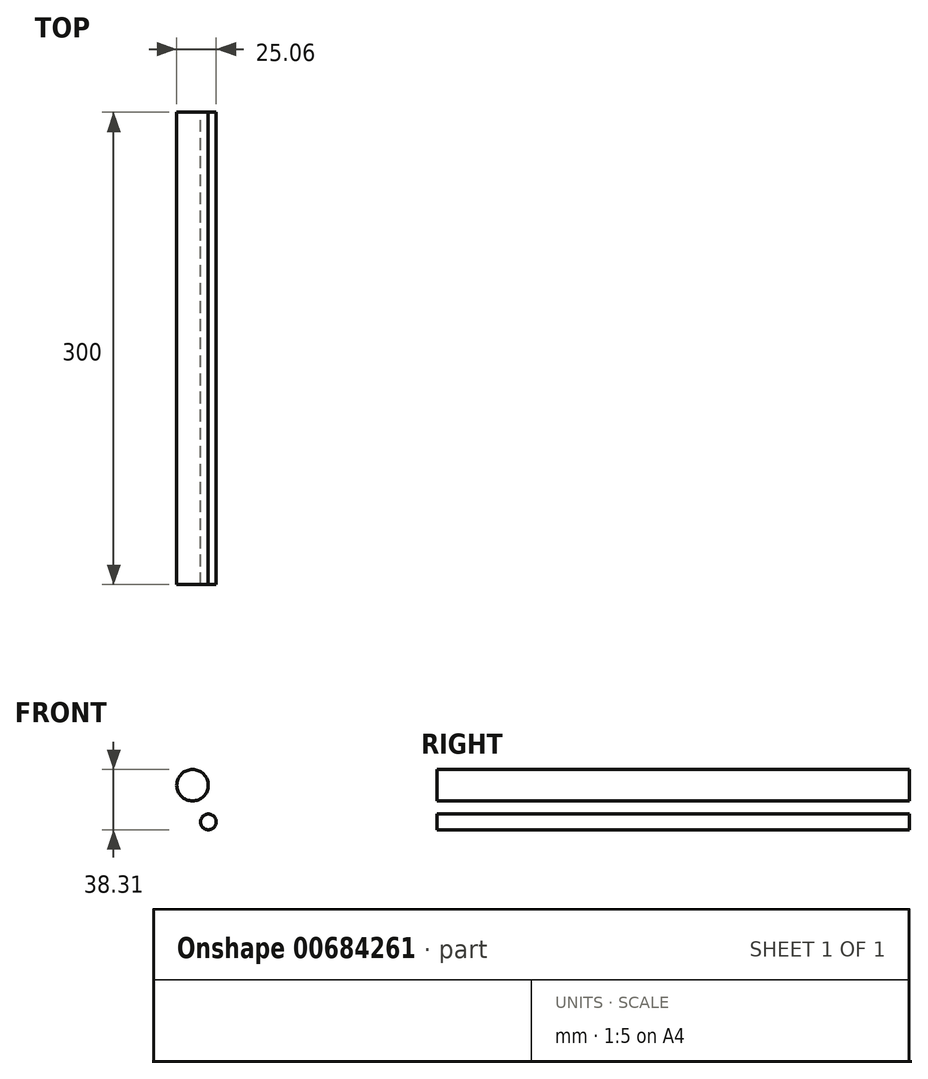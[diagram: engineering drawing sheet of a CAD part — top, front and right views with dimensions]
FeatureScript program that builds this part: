
annotation { "Feature Type Name" : "Feature", "Feature Type Description" : "" }
export const myFeature = defineFeature(function(context is Context, id is Id, definition is map)
    precondition{}
    {
        {
            var Q0;
            Q0=qCreatedBy(makeId("Front.planeOp"),FACE);
            var sketch = newSketch(context, id + "F0", { "sketchPlane" : qUnion([Q0])});
            skCircle(sketch, "E0", {"center": v(0, 0) * mm, "radius": 5 * mm});
            skCircle(sketch, "E1", {"center": v(-10.06, 23.3) * mm, "radius": 10 * mm});
            skSolve(sketch);
        }
        {
            var Q0;
            Q0 = qSketchRegion(id + "F0", true);
            extrude(context, id + "F1", {"entities" : qUnion([Q0]), "endBound" : BoundingType.SYMMETRIC, "depth" : 300 * mm, "offsetDistance" : 25 * mm});
        }
    });
